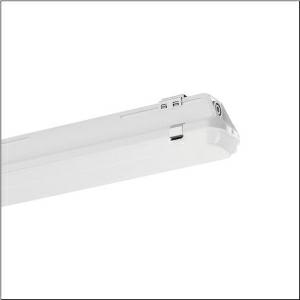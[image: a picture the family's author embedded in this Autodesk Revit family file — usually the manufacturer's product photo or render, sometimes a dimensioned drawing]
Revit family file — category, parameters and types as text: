
# Revit family: monsun_11_emergency_51fp20dp467l3h
name_source: partatom
category: Lighting Fixtures
units: mm (PartAtom-declared; Revit-internal decimal feet)

## family parameters
Cut with Voids When Loaded = No
Host = Face
Light Source = No
Part Type = Normal
Room Calculation Point = No
Round Connector Dimension = Use Diameter
Shared = No

## types (1)
- --- (1 x LED, 910 lm, 6.2 W, 4000K)
    Apparent Load = 6 VA
    CIE Flux Codes = 45 75 93 94 100
    Color Rendering = 80
    Color Temperature = 4000K
    Default Elevation = 1800 mm
    Description = Monsun 11 emergency, damp-proof luminaire, chain hanger, primary optical cover: enclosure, of PC, light emission: direct distribution, primary light characteristic: symmetric, installation type: suspended mounting, surface-mounted, horizontal mounting, vertical mounting, LED, rated luminous flux: 5.450lm, luminous efficacy: 173lm/W, light colour: 840, colour temperature: 4000K, control gear: DALI 2, with terminal, 5+3-pole, max. 2.5mm², mains connection: 220..240V, AC, 50/60Hz, rated input power: 35W, control gear: single battery element, battery: LiFePO4, 9Ah, luminaire housing, of glass-fibre reinforced polyester, uncoated, bright grey, incl. chain hanger, length: 1.590mm, width: 90mm, height: 88mm, clip for enclosure, of stainless steel (V2A), ceiling mounting element, of stainless steel (V2A), chain hanger, of stainless steel (V2A), protection rating (complete): IP66, insulation class (complete): insulation class I (protective earthing), certification: CE, UKCA, protection symbol: D, impact resistance: IK08, permissible operating ambient temperature: +5..+35°C, standard: EN 50419, EN 60598-2-1, EN 60598-2-22, contact your sales advisor before using the luminaires in applications with unclear chemical exposure, large temperature fluctuations or condensation-forming humidity, LABS conformity tested according to VDMA 24364:2018-05, no direct snow, no direct sun, no direct rain, for indoor or canopied outdoor use, corresponds to IFS (International Featured Standards) requirements for safety and quality in the food industry, packaging unit: 1 piece
    Height = 89 mm
    Lamp = 1 x LED
    Lamp Light Flux = 910 lm
    Lamp Power = 6.2 W
    Lamp count = 1
    Length = 1590 mm
    Luminous efficacy = 147 lm/W
    Manufacturer = Siteco
    ModVariant = No
    Model = 51FP20DP467L3H
    Mounting Place = Ceiling
    Mounting Type = Surface mounted
    Number of Poles = 1
    OnlyDefault = Yes
    Power Factor = 1
    Product Name = Monsun 11 emergency
    Product group = damp-proof luminaire
    ProductGroupID = 300
    Protection Class = Protection class I
    Protection Degree = IP 66
    RLX_Detail_Level = 1
    RLX_Emergency_Light_Flux = 0 lm
    RLX_Emergency_Type = 0
    RLX_Emergency_Type_DB = No
    RlxData = <blob elided: 92357 chars, md5=7f398452>
    Socket = socket
    Standby Power = 0 W
    System Light Flux = 910 lm
    System Power = 6 W
    Type Comments = : emergency light operation: 3 h
    Type Image = l_1349237.jpg
    URL = http://relux.com
    VarID = @adj_034161
    Voltage = 0 V
    Weight = 0.00 kg
    Width = 90 mm

## geometry (parser evidence)
native form markers: Blend x4, Sweep x12
no freeform markers — native parametric forms only
